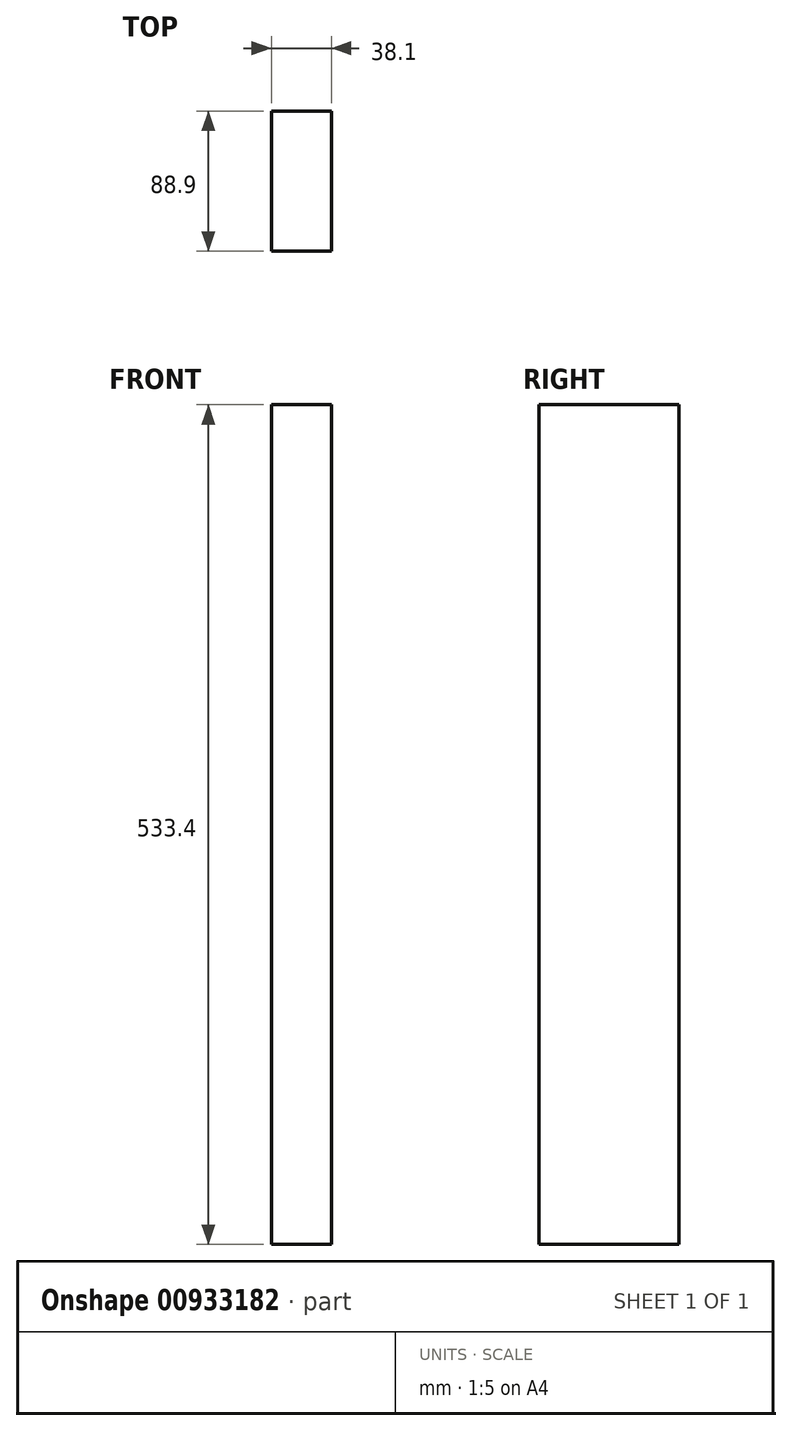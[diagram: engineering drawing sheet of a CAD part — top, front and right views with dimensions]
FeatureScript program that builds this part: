
annotation { "Feature Type Name" : "Feature", "Feature Type Description" : "" }
export const myFeature = defineFeature(function(context is Context, id is Id, definition is map)
    precondition{}
    {
        {
            var Q0;
            Q0=qCreatedBy(makeId("Top.planeOp"),FACE);
            var sketch = newSketch(context, id + "F0", { "sketchPlane" : qUnion([Q0])});
            skLineSegment(sketch, "E0.bottom", {"start": v(19.05, 44.45) * mm, "end": v(-19.05, 44.45) * mm});
            skLineSegment(sketch, "E0.top", {"start": v(19.05, -44.45) * mm, "end": v(-19.05, -44.45) * mm});
            skLineSegment(sketch, "E0.left", {"start": v(19.05, 44.45) * mm, "end": v(19.05, -44.45) * mm});
            skLineSegment(sketch, "E0.right", {"start": v(-19.05, 44.45) * mm, "end": v(-19.05, -44.45) * mm});
            skPoint(sketch, "E0.middle", {"position": v(0, 0) * mm});
            skSolve(sketch);
        }
        {
            var Q0;
            Q0 = qSketchRegion(id + "F0", true);
            extrude(context, id + "F1", {"entities" : qUnion([Q0]), "depth" : 533.4 * mm, "offsetDistance" : 25.4 * mm});
        }
    });
